# Revit family: subgril
name_source: partatom
category: 制気口
units: mm (PartAtom-declared; Revit-internal decimal feet)

## family parameters
OmniClass タイトル = Diffusers, Registers, and Grilles
OmniClass 番号 = 23.75.70.21.27.11
パーツ タイプ = 標準
ロード時にボイドで切り取り = いいえ
丸型コネクタ寸法 = 直径を使用
作業面ベース = いいえ
共有 = いいえ
常に垂直 = はい
部屋計算ポイント = はい

## types (2) — shared parameters
IfcExportAs = IfcAirTerminalType
Uniclass2015Title = Air grilles
Uniclass2015Version = Systems v1.9
グリルマテリアル = 合成樹脂(白)
仕様書バージョン = Version1.0
本体マテリアル = 合成樹脂(黒)
法定耐用年数 = 15
矢印なし吸込表記 = はい
矢印表記 = いいえ

## per-type parameters (varying)
| type | EAサイズ_D | IfcExportType | OmniClassCode | Uniclass2015Code | 企業コード | 呼称 | 積算_科目 | 符号 | 製造元 |
| H | 130  [stored 0.426509 ft] | REGISTER | 23-33 49 25 11 | Pr_70_65_04_03 |  | ユニバーサル形吸込口_H |  | H |  |
| HS | 97  [stored 0.318241 ft] | GRILLE | 23-33 49 23 11 | Pr_70_65_04_28 | 108420 |  | 2 換気設備 |  | 三菱電機株式会社 |

note: [stored X ft] marks values corroborated as IEEE doubles in the binary element streams (Revit-internal decimal feet)

## geometry (parser evidence)
native form markers: Blend x2
no freeform markers — native parametric forms only
